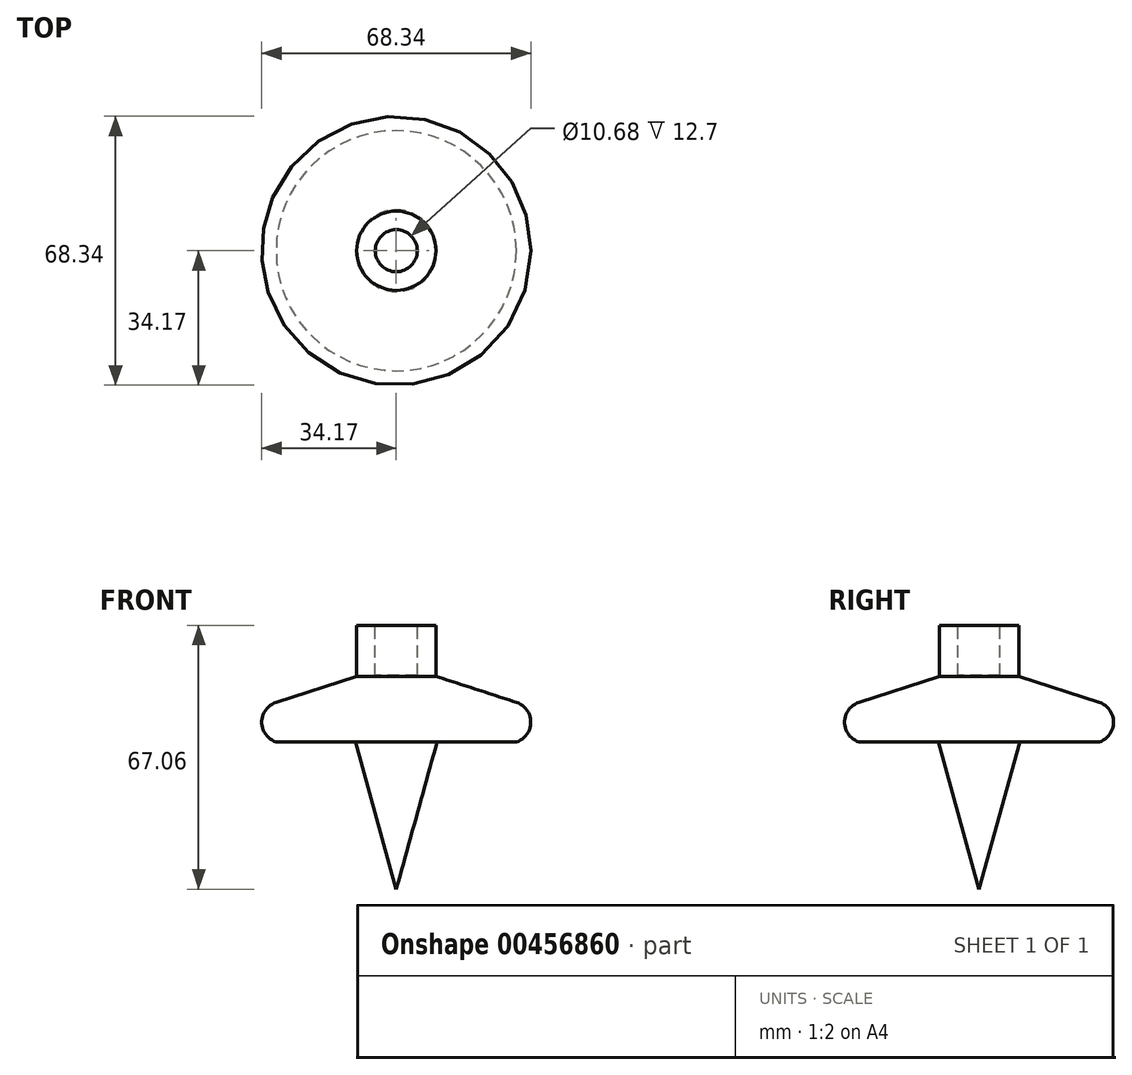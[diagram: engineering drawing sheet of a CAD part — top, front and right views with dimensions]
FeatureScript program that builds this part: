
annotation { "Feature Type Name" : "Feature", "Feature Type Description" : "" }
export const myFeature = defineFeature(function(context is Context, id is Id, definition is map)
    precondition{}
    {
        {
            var Q0;
            Q0=qCreatedBy(makeId("Front.planeOp"),FACE);
            var sketch = newSketch(context, id + "F0", { "sketchPlane" : qUnion([Q0])});
            skLineSegment(sketch, "E0", {"start": v(0, 0) * mm, "end": v(10.36, 37.41) * mm});
            skLineSegment(sketch, "E1", {"start": v(10.36, 37.41) * mm, "end": v(30.5, 37.41) * mm});
            skLineSegment(sketch, "E2", {"start": v(30.5, 37.41) * mm, "end": v(30.5, 47.49) * mm});
            skLineSegment(sketch, "E3", {"start": v(30.5, 47.49) * mm, "end": v(10.07, 54.1) * mm});
            skLineSegment(sketch, "E4", {"start": v(10.07, 54.1) * mm, "end": v(10.07, 67.06) * mm});
            skLineSegment(sketch, "E5", {"start": v(10.07, 67.06) * mm, "end": v(0, 67.06) * mm});
            skLineSegment(sketch, "E6", {"start": v(0, 67.06) * mm, "end": v(0, 0) * mm});
            skArc(sketch, "E7", {"start": v(30.5, 37.41) * mm, "mid": v(34.17, 42.45) * mm, "end": v(30.5, 47.49) * mm});
            skSolve(sketch);
        }
        {
            var Q0;
            Q0 = qSketchRegion(id + "F0", true);
            var Q1;
            Q1=sQuery(id+"F0.wireOp",EDGE,"E6");
            revolve(context, id + "F1", {"entities" : qUnion([Q0]), "axis" : qUnion([Q1]), "revolveType" : RevolveType.FULL});
        }
        {
            var Q0;
            Q0=makeQuery(id+"F1.opRevolve","SWEPT_FACE",FACE,{"disambiguationData":[OSD([sQuery(id+"F0.wireOp",EDGE,"E5")])]});
            var sketch = newSketch(context, id + "F2", { "sketchPlane" : qUnion([Q0])});
            skCircle(sketch, "E8", {"center": v(0, 0) * mm, "radius": 5.34 * mm});
            skSolve(sketch);
        }
        {
            var Q0;
            Q0=makeQuery(id+"F2.imprint","IMPRINT",FACE,{"disambiguationData":[TD([[makeQuery(id+"F2.imprint","IMPRINT",EDGE,{"derivedFrom":sQuery(id+"F2.wireOp",EDGE,"E8")}),1.0]])]});
            extrude(context, id + "F3", {"entities" : qUnion([Q0]), "operationType" : NewBodyOperationType.REMOVE, "oppositeDirection" : true, "depth" : 12.7 * mm});
        }
    });
